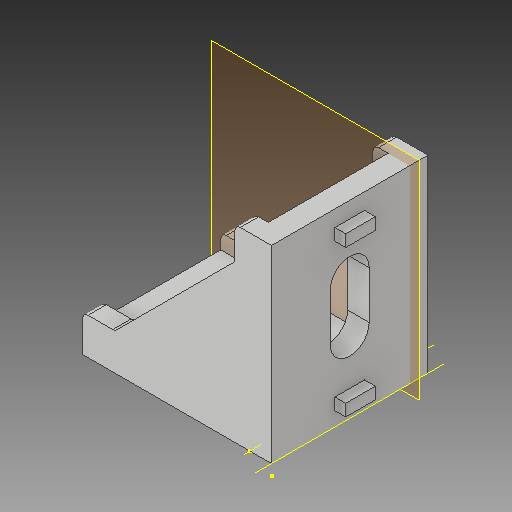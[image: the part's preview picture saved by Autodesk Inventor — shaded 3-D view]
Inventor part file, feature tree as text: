
AUTODESK INVENTOR PART (.ipt)
format: ipt  version: 2018 (Build 220112000, 112)  size: 187,904 bytes
history: native  units: mm
features: sketch x8, other x5, plane x1
ambient origin geometry x8: Origin, YZ Plane, XZ Plane, XY Plane, X Axis, Y Axis, Z Axis, Center Point
bodies: Solid1 (feature_tree)
feature tree (14):
  other  "30mm Bracket_CPY_MIR2_MIR.ipt"
  other  "Solid1::30mm Bracket_CPY_MIR2_MIR.ipt"
  other  "TaggingFeature1"
  sketch  "Sketch1"  dims[d0=10.0mm]
  sketch  "Sketch2"
  sketch  "Sketch3"
  sketch  "Sketch4"
  sketch  "Sketch5"
  sketch  "Sketch7"
  sketch  "Sketch9"
  sketch  "Sketch10"
  plane  "Work Plane1"
  other  "Work Axis1"
  other  "Work Axis2"
